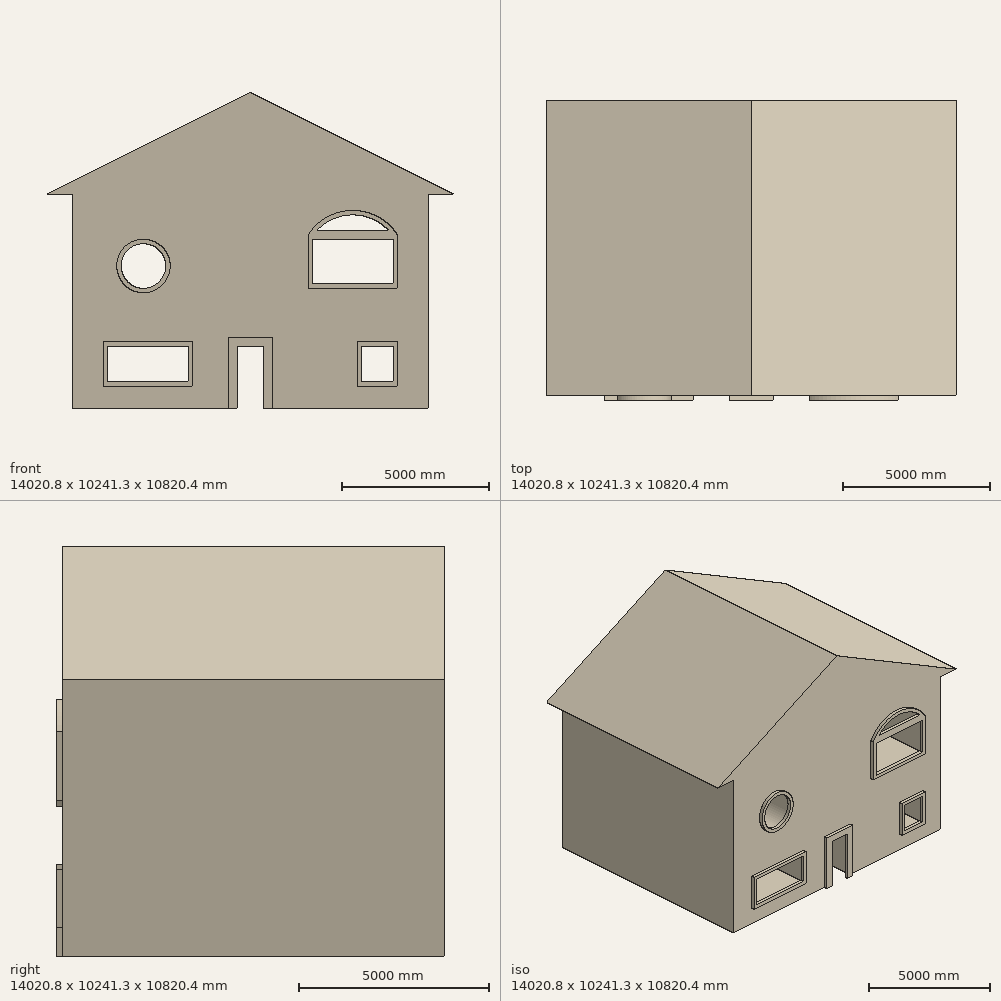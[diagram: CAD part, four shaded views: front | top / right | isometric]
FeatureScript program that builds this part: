
annotation { "Feature Type Name" : "Feature", "Feature Type Description" : "" }
export const myFeature = defineFeature(function(context is Context, id is Id, definition is map)
    precondition{}
    {
        {
            var Q0;
            Q0=qCreatedBy(makeId("Front.planeOp"),FACE);
            var sketch = newSketch(context, id + "F0", { "sketchPlane" : qUnion([Q0])});
            skLineSegment(sketch, "E0", {"start": v(0, 0) * mm, "end": v(-6096, 0) * mm});
            skLineSegment(sketch, "E1", {"start": v(0, 0) * mm, "end": v(6096, 0) * mm});
            skLineSegment(sketch, "E2", {"start": v(0, 0) * mm, "end": v(0, 3048) * mm, "construction": true});
            skLineSegment(sketch, "E3", {"start": v(-6096, 0) * mm, "end": v(0, 3048) * mm});
            skLineSegment(sketch, "E4", {"start": v(0, 3048) * mm, "end": v(6096, 0) * mm});
            skLineSegment(sketch, "E5", {"start": v(6096, 0) * mm, "end": v(7010.4, 0) * mm});
            skLineSegment(sketch, "E6", {"start": v(-6096, 0) * mm, "end": v(-7010.4, 0) * mm});
            skLineSegment(sketch, "E7", {"start": v(0, 3048) * mm, "end": v(0, 3505.2) * mm});
            skLineSegment(sketch, "E8", {"start": v(0, 3505.2) * mm, "end": v(7010.4, 0) * mm});
            skLineSegment(sketch, "E9", {"start": v(0, 3505.2) * mm, "end": v(-7010.4, 0) * mm});
            skLineSegment(sketch, "E10", {"start": v(-6096, 0) * mm, "end": v(-6096, -7315.2) * mm});
            skLineSegment(sketch, "E11", {"start": v(-6096, -7315.2) * mm, "end": v(6096, -7315.2) * mm});
            skLineSegment(sketch, "E12", {"start": v(6096, -7315.2) * mm, "end": v(6096, 0) * mm});
            skLineSegment(sketch, "E13", {"start": v(-6096, -7315.2) * mm, "end": v(-6096, -7620) * mm});
            skLineSegment(sketch, "E14", {"start": v(6096, -7620) * mm, "end": v(6096, -7315.2) * mm});
            skLineSegment(sketch, "E15", {"start": v(-6096, -7620) * mm, "end": v(6096, -7620) * mm});
            skLineSegment(sketch, "E16", {"start": v(0, -7315.2) * mm, "end": v(-457.2, -7315.2) * mm});
            skLineSegment(sketch, "E17", {"start": v(457.2, -7315.2) * mm, "end": v(0, -7315.2) * mm});
            skLineSegment(sketch, "E18", {"start": v(-457.2, -7315.2) * mm, "end": v(-457.2, -5181.6) * mm});
            skLineSegment(sketch, "E19", {"start": v(228.6, -7315.2) * mm, "end": v(0, -7315.2) * mm});
            skLineSegment(sketch, "E20", {"start": v(0, -7315.2) * mm, "end": v(457.2, -7315.2) * mm});
            skLineSegment(sketch, "E21", {"start": v(457.2, -7315.2) * mm, "end": v(457.2, -5181.6) * mm});
            skLineSegment(sketch, "E22", {"start": v(457.2, -5181.6) * mm, "end": v(-457.2, -5181.6) * mm});
            skLineSegment(sketch, "E23", {"start": v(-4876.8, -5181.6) * mm, "end": v(-4876.8, -6400.8) * mm});
            skLineSegment(sketch, "E24", {"start": v(-4876.8, -5181.6) * mm, "end": v(-2133.6, -5181.6) * mm});
            skLineSegment(sketch, "E25", {"start": v(-4876.8, -6400.8) * mm, "end": v(-2133.6, -6400.8) * mm});
            skLineSegment(sketch, "E26", {"start": v(-2133.6, -6400.8) * mm, "end": v(-2133.6, -5181.6) * mm});
            skLineSegment(sketch, "E27", {"start": v(3810, -5181.6) * mm, "end": v(3810, -6400.8) * mm});
            skLineSegment(sketch, "E28", {"start": v(3810, -6400.8) * mm, "end": v(4876.8, -6400.8) * mm});
            skLineSegment(sketch, "E29", {"start": v(4876.8, -6400.8) * mm, "end": v(4876.8, -5181.6) * mm});
            skLineSegment(sketch, "E30", {"start": v(4876.8, -5181.6) * mm, "end": v(3810, -5181.6) * mm});
            skPoint(sketch, "E31.endSnap0", {"position": v(4343.4, -6400.8) * mm});
            skLineSegment(sketch, "E32.0", {"start": v(-5029.2, -5029.2) * mm, "end": v(-1981.2, -5029.2) * mm});
            skLineSegment(sketch, "E32.1", {"start": v(-5029.2, -5029.2) * mm, "end": v(-5029.2, -6553.2) * mm});
            skLineSegment(sketch, "E32.2", {"start": v(-5029.2, -6553.2) * mm, "end": v(-1981.2, -6553.2) * mm});
            skLineSegment(sketch, "E32.3", {"start": v(-1981.2, -6553.2) * mm, "end": v(-1981.2, -5029.2) * mm});
            skLineSegment(sketch, "E33.0", {"start": v(3657.6, -6553.2) * mm, "end": v(5029.2, -6553.2) * mm});
            skLineSegment(sketch, "E33.1", {"start": v(3657.6, -5029.2) * mm, "end": v(3657.6, -6553.2) * mm});
            skLineSegment(sketch, "E33.2", {"start": v(5029.2, -5029.2) * mm, "end": v(3657.6, -5029.2) * mm});
            skLineSegment(sketch, "E33.3", {"start": v(5029.2, -6553.2) * mm, "end": v(5029.2, -5029.2) * mm});
            skLineSegment(sketch, "E34.0", {"start": v(-762, -7315.2) * mm, "end": v(-762, -4876.8) * mm});
            skLineSegment(sketch, "E34.1", {"start": v(762, -4876.8) * mm, "end": v(-762, -4876.8) * mm});
            skLineSegment(sketch, "E34.2", {"start": v(762, -7315.2) * mm, "end": v(762, -4876.8) * mm});
            skCircle(sketch, "E35", {"center": v(-3657.6, -2438.4) * mm, "radius": 914.4 * mm});
            skCircle(sketch, "E36.0", {"center": v(-3657.6, -2438.4) * mm, "radius": 762 * mm});
            skLineSegment(sketch, "E37", {"start": v(2133.6, -3048) * mm, "end": v(2133.6, -1524) * mm});
            skLineSegment(sketch, "E38", {"start": v(2133.6, -1524) * mm, "end": v(4876.8, -1524) * mm});
            skLineSegment(sketch, "E39", {"start": v(4876.8, -1524) * mm, "end": v(4876.8, -3048) * mm});
            skLineSegment(sketch, "E40", {"start": v(2133.6, -3048) * mm, "end": v(4876.8, -3048) * mm});
            skLineSegment(sketch, "E41.0", {"start": v(1981.2, -1371.6) * mm, "end": v(5029.2, -1371.6) * mm});
            skLineSegment(sketch, "E41.1", {"start": v(1981.2, -3200.4) * mm, "end": v(1981.2, -1371.6) * mm});
            skLineSegment(sketch, "E41.2", {"start": v(1981.2, -3200.4) * mm, "end": v(5029.2, -3200.4) * mm});
            skLineSegment(sketch, "E41.3", {"start": v(5029.2, -1371.6) * mm, "end": v(5029.2, -3200.4) * mm});
            skArc(sketch, "E42", {"start": v(5029.2, -1371.6) * mm, "mid": v(3505.2, -535.07) * mm, "end": v(1981.2, -1371.6) * mm});
            skArc(sketch, "E43.0", {"start": v(4720.24, -1219.2) * mm, "mid": v(3505.2, -687.47) * mm, "end": v(2290.16, -1219.2) * mm});
            skLineSegment(sketch, "E43.1", {"start": v(2290.16, -1219.2) * mm, "end": v(4720.24, -1219.2) * mm});
            skSolve(sketch);
        }
        {
            var Q0;
            Q0=makeQuery(id+"F0.imprint","IMPRINT",FACE,{"disambiguationData":[TD([[makeQuery(id+"F0.imprint","IMPRINT",EDGE,{"derivedFrom":sQuery(id+"F0.wireOp",EDGE,"E35")}),1.0]])]});
            var Q1;
            Q1=makeQuery(id+"F0.imprint","IMPRINT",FACE,{"disambiguationData":[TD([[makeQuery(id+"F0.imprint","IMPRINT",EDGE,{"derivedFrom":sQuery(id+"F0.wireOp",EDGE,"E23")}),-1.0]])]});
            var Q2;
            {var subQ0=sQuery(id+"F0.wireOp",EDGE,"E18");Q2=makeQuery(id+"F0.imprint","IMPRINT",FACE,{"disambiguationData":[TD([[makeQuery(id+"F0.imprint","IMPRINT",EDGE,{"derivedFrom":subQ0}),1.0]])]});}
            var Q3;
            Q3=makeQuery(id+"F0.imprint","IMPRINT",FACE,{"disambiguationData":[TD([[makeQuery(id+"F0.imprint","IMPRINT",EDGE,{"derivedFrom":sQuery(id+"F0.wireOp",EDGE,"E37")}),1.0]])]});
            var Q4;
            Q4=makeQuery(id+"F0.imprint","IMPRINT",FACE,{"disambiguationData":[TD([[makeQuery(id+"F0.imprint","IMPRINT",EDGE,{"derivedFrom":sQuery(id+"F0.wireOp",EDGE,"E41.0")}),1.0]])]});
            var Q5;
            Q5=makeQuery(id+"F0.imprint","IMPRINT",FACE,{"disambiguationData":[TD([[makeQuery(id+"F0.imprint","IMPRINT",EDGE,{"derivedFrom":sQuery(id+"F0.wireOp",EDGE,"E27")}),-1.0]])]});
            extrude(context, id + "F1", {"entities" : qUnion([Q0, Q1, Q2, Q3, Q4, Q5]), "depth" : 152.4 * mm, "offsetDistance" : 30.48 * mm});
        }
        {
            var Q0;
            Q0=makeQuery(id+"F0.imprint","IMPRINT",FACE,{"disambiguationData":[TD([[makeQuery(id+"F0.imprint","IMPRINT",EDGE,{"derivedFrom":sQuery(id+"F0.wireOp",EDGE,"E3")}),1.0]])]});
            var Q1;
            Q1=makeQuery(id+"F0.imprint","IMPRINT",FACE,{"disambiguationData":[TD([[makeQuery(id+"F0.imprint","IMPRINT",EDGE,{"derivedFrom":sQuery(id+"F0.wireOp",EDGE,"E0")}),-1.0]])]});
            var Q2;
            Q2=makeQuery(id+"F0.imprint","IMPRINT",FACE,{"disambiguationData":[TD([[makeQuery(id+"F0.imprint","IMPRINT",EDGE,{"derivedFrom":sQuery(id+"F0.wireOp",EDGE,"E4")}),1.0]])]});
            var Q3;
            Q3=makeQuery(id+"F0.imprint","IMPRINT",FACE,{"disambiguationData":[TD([[makeQuery(id+"F0.imprint","IMPRINT",EDGE,{"derivedFrom":sQuery(id+"F0.wireOp",EDGE,"E0")}),1.0]])]});
            extrude(context, id + "F2", {"entities" : qUnion([Q0, Q1, Q2, Q3]), "oppositeDirection" : true, "depth" : 10088.88 * mm, "offsetDistance" : 30.48 * mm});
        }
    });
